# Revit family: Power-ModularDevices-GEWISS-90AM-SOCKET_OUTLET_DIN_DEU
name_source: partatom
category: Apparecchi elettrici
revit_build: Autodesk Revit 2016 (Build: 20161004_0715(x64)
units: mm (PartAtom-declared; Revit-internal decimal feet)

## family parameters
Condiviso = No
Host = Superficie
Mantenere orientamento annotazione = Sì
Numero OmniClass = 23.80.50.11
Punto di calcolo locali = Sì
Quota connettore circolare = Usa diametro
Taglio con vuoti quando caricato = No
Tipo di parte = Normale
Titolo OmniClass = Switches and Receptacles

## types (1)
- Power-ModularDevices-GEWISS-90AM-SOCKET_OUTLET_DIN_DEU
    Catalogue = POWER
    Catalogue Range = 90 AM
    Descrizione = DIN RAIL SOCKET GER.STD -2P+E 16A - 2,5M
    EAN code = 8011564441729
    Electrocod = 140
    Finitura = <Per categoria>
    IDF = ca512cc2-6dfa-4e8c-867a-303be78aa01b
    IDT = 218c7963-caa2-4db4-bed7-6c0ad32bbe90
    Immagine tipo = GW96522.jpg
    Installation = DIN rail
    Modello = GW96522
    No. Chorus modules = 2,5
    Number of poles = 2P+E
    Produttore = GEWISS S.p.A.
    Prospetto di default = 1219 mm
    Rated current (In) = 16 A
    Rated voltage = 250Vac
    Standard = German
    Technical sheet = https://www.gewiss.com
    URL = https://www.gewiss.com
    Version file RFA = 18.0
